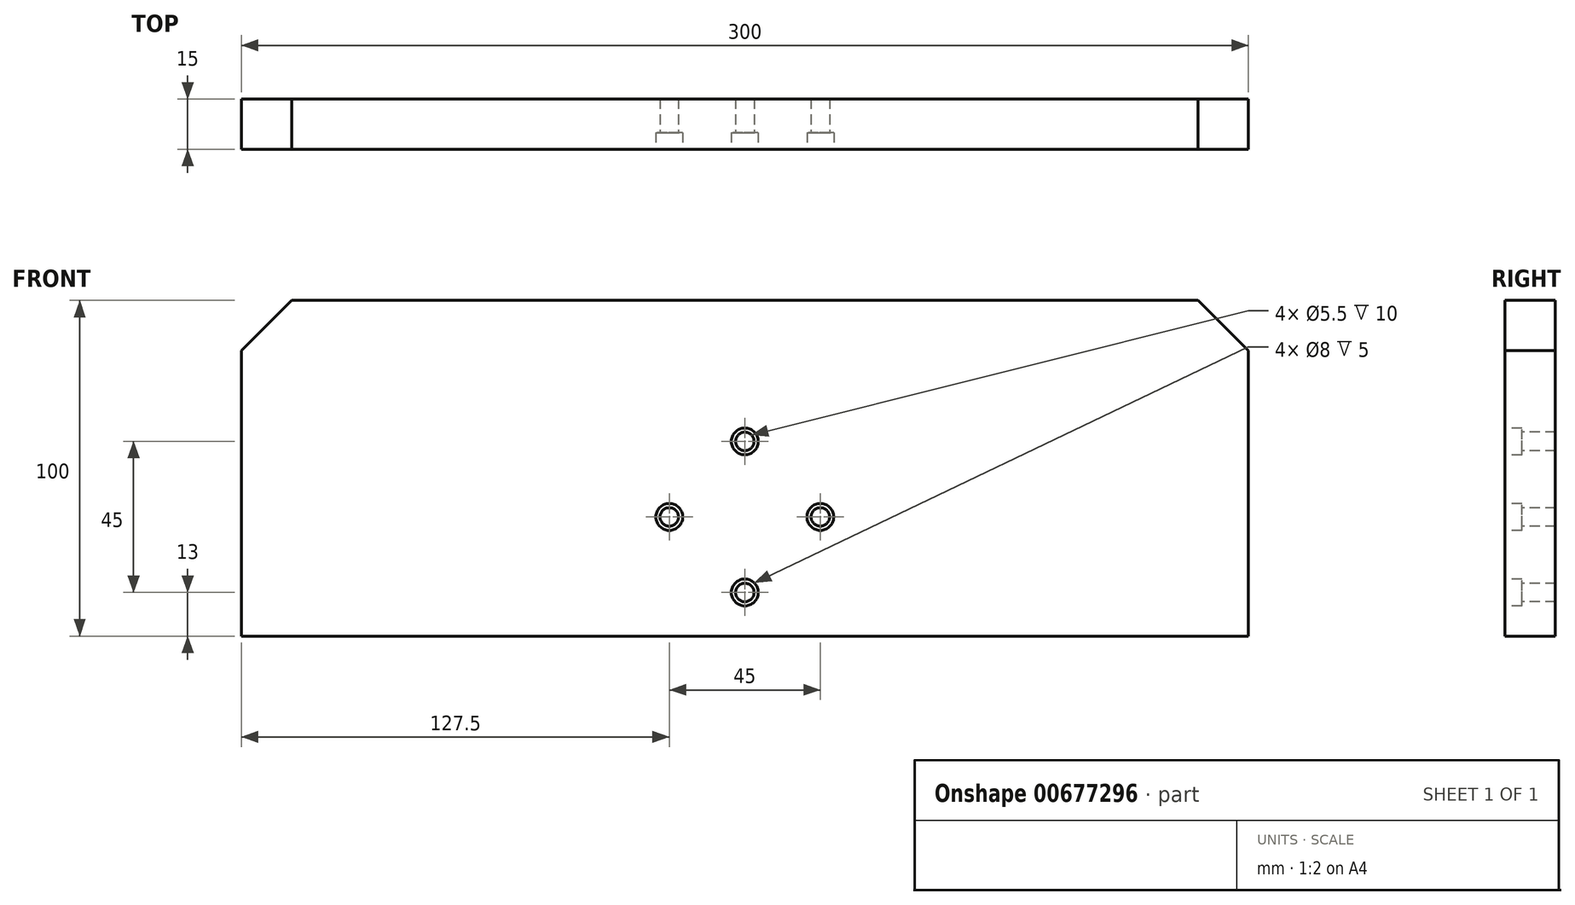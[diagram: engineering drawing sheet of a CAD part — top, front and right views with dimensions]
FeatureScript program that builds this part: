
annotation { "Feature Type Name" : "Feature", "Feature Type Description" : "" }
export const myFeature = defineFeature(function(context is Context, id is Id, definition is map)
    precondition{}
    {
        {
            var Q0;
            Q0=qCreatedBy(makeId("Front.planeOp"),FACE);
            var sketch = newSketch(context, id + "F0", { "sketchPlane" : qUnion([Q0])});
            skLineSegment(sketch, "E0.bottom", {"start": v(0, 0) * mm, "end": v(300, 0) * mm});
            skLineSegment(sketch, "E0.top", {"start": v(0, 100) * mm, "end": v(300, 100) * mm});
            skLineSegment(sketch, "E0.left", {"start": v(0, 0) * mm, "end": v(0, 100) * mm});
            skLineSegment(sketch, "E0.right", {"start": v(300, 0) * mm, "end": v(300, 100) * mm});
            skSolve(sketch);
        }
        {
            var Q0;
            Q0=makeQuery(id+"F0.imprint","IMPRINT",FACE,{"disambiguationData":[TD([[makeQuery(id+"F0.imprint","IMPRINT",EDGE,{"derivedFrom":sQuery(id+"F0.wireOp",EDGE,"E0.bottom")}),1.0]])]});
            extrude(context, id + "F1", {"entities" : qUnion([Q0]), "oppositeDirection" : true, "depth" : 15 * mm, "offsetDistance" : 25 * mm});
        }
        {
            var Q0;
            Q0=makeQuery(id+"F1.opExtrude","CAP_FACE",FACE,{"disambiguationData":[OSD([sQuery(id+"F0.wireOp",EDGE,"E0.bottom"),sQuery(id+"F0.wireOp",EDGE,"E0.top"),sQuery(id+"F0.wireOp",EDGE,"E0.left"),sQuery(id+"F0.wireOp",EDGE,"E0.right")])],"isStart":true});
            var sketch = newSketch(context, id + "F2", { "sketchPlane" : qUnion([Q0])});
            skLineSegment(sketch, "E1", {"start": v(0, 0) * mm, "end": v(150, 0) * mm, "construction": true});
            skLineSegment(sketch, "E2", {"start": v(150, 0) * mm, "end": v(150, 13) * mm, "construction": true});
            skLineSegment(sketch, "E3", {"start": v(150, 13) * mm, "end": v(150, 58) * mm, "construction": true});
            skLineSegment(sketch, "E4", {"start": v(150, 58) * mm, "end": v(150, 35.5) * mm, "construction": true});
            skLineSegment(sketch, "E5", {"start": v(150, 35.5) * mm, "end": v(172.5, 35.5) * mm, "construction": true});
            skLineSegment(sketch, "E6", {"start": v(172.5, 35.5) * mm, "end": v(127.5, 35.5) * mm, "construction": true});
            skCircle(sketch, "E7", {"center": v(150, 58) * mm, "radius": 3 * mm});
            skCircle(sketch, "E8", {"center": v(172.5, 35.5) * mm, "radius": 3 * mm});
            skCircle(sketch, "E9", {"center": v(127.5, 35.5) * mm, "radius": 3 * mm});
            skCircle(sketch, "E10", {"center": v(150, 13) * mm, "radius": 3 * mm});
            skSolve(sketch);
        }
        {
            var Q0;
            Q0=makeQuery(id+"F1.opExtrude","SWEPT_EDGE",EDGE,{"disambiguationData":[OSD([sQuery(id+"F0.wireOp",EDGE,"E0.top"),sQuery(id+"F0.wireOp",EDGE,"E0.left")])]});
            var Q1;
            Q1=makeQuery(id+"F1.opExtrude","SWEPT_EDGE",EDGE,{"disambiguationData":[OSD([sQuery(id+"F0.wireOp",EDGE,"E0.top"),sQuery(id+"F0.wireOp",EDGE,"E0.right")])]});
            chamfer(context, id + "F3", {"entities" : qUnion([Q0, Q1]), "width" : 15 * mm, "tangentPropagation" : true});
        }
        {
            var Q0;
            Q0=sQuery(id+"F2.wireOp",VERTEX,"E9.center");
            var Q1;
            Q1=sQuery(id+"F2.wireOp",VERTEX,"E4.start");
            var Q2;
            Q2=sQuery(id+"F2.wireOp",VERTEX,"E8.center");
            var Q3;
            Q3=sQuery(id+"F2.wireOp",VERTEX,"E3.start");
            var Q4;
            Q4=makeQuery(id+"F1.opExtrude","SWEPT_BODY",BODY,{"disambiguationData":[OSD([sQuery(id+"F0.wireOp",EDGE,"E0.bottom"),sQuery(id+"F0.wireOp",EDGE,"E0.top"),sQuery(id+"F0.wireOp",EDGE,"E0.left"),sQuery(id+"F0.wireOp",EDGE,"E0.right")])]});
            hole(context, id + "F4", {"style" : HoleStyle.C_BORE, "endStyle" : HoleEndStyle.THROUGH, "holeDiameter" : 5.5 * mm, "cBoreDiameter" : 8 * mm, "cBoreDepth" : 5 * mm, "majorDiameter" : 5 * mm, "isTappedThrough" : true, "tappedDepth" : 12 * mm, "tapClearance" : 3, "locations" : qUnion([Q0, Q1, Q2, Q3]), "scope" : qUnion([Q4])});
        }
    });
